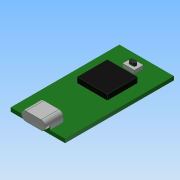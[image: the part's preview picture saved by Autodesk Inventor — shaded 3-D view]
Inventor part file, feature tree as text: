
AUTODESK INVENTOR PART (.ipt)
format: ipt  version: 2015 (Build 190159000, 159)  size: 141,312 bytes
history: native  units: mm
features: extrude x5, sketch x5, fillet x1, projected_geometry x1
ambient origin geometry x8: Origin, YZ Plane, XZ Plane, XY Plane, X Axis, Y Axis, Z Axis, Center Point
bodies: Volumenkörper1 (feature_tree)
feature tree (12):
  extrude  "Extrusion1"  Depth=36.0mm
  extrude  "Extrusion5"  Depth=10.0mm
  fillet  "Rundung1"  Radius=8.0mm
  extrude  "Extrusion3"  Depth=4.0mm
  extrude  "Extrusion4"  Depth=3.0mm
  extrude  "Extrusion2"  Depth=2.2mm
  sketch  "Skizze1"  dims[d0=18.0mm d1=36.0mm]
  sketch  "Skizze2"  dims[d2=1.2mm d3=0.0mm d4=10.0mm d5=8.0mm]
  sketch  "Skizze3"  dims[d6=1.8mm d7=0.0mm d8=4.0mm]
  sketch  "Skizze4"  dims[d9=3.0mm d10=3.0mm]
  projected_geometry  "Projizierte Kontur1"
  sketch  "Skizze5"  dims[d11=1.2mm d12=0.0mm d13=2.2mm d14=1.2mm d15=1.0mm d16=0.0mm d17=8.0mm d18=6.0mm d19=4.5mm d20=3.0mm d21=0.0mm d22=1.5mm]
